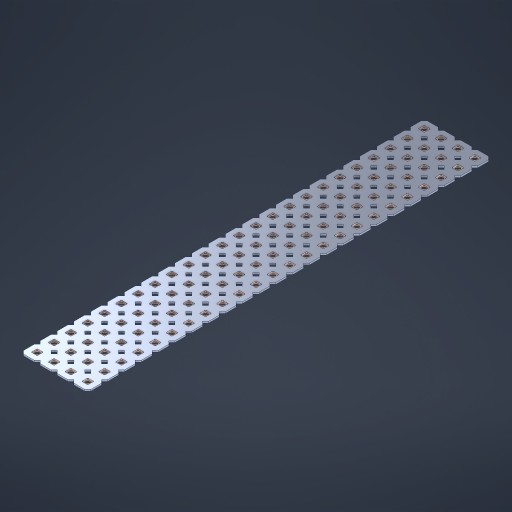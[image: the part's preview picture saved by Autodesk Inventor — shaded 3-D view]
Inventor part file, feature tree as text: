
AUTODESK INVENTOR PART (.ipt)
format: ipt  version: 2023 (Build 270158000, 158)  size: 1,368,064 bytes
history: native  units: in
note: dims shown in document units (in); Inventor stores cm internally (conversion verified against a paired STEP export)
features: other x97, extrude x95, sketch x2, pattern_linear x1
ambient origin geometry x8: Origin, YZ Plane, XZ Plane, XY Plane, X Axis, Y Axis, Z Axis, Center Point
bodies: Solid1 (feature_tree), Body (feature_tree)
feature tree (195):
  pattern_linear  "Rectangular Pattern1"  Spacing1=0.09in  [1 undecoded]
  sketch  "Sketch1"  dims[d1=0.5in]
  sketch  "Sketch2"  dims[d2=0.182in d3=0.09in d4=0.09in d5=0.09in d6=0.09in d7=0.09in d8=0.09in d9=0.09in d10=0.09in d11=0.02in d13=0.0in d14=0.172in d15=0.0625in d16=0.0in d19=0.5in d22=0.5in]
  other  "Srf1"
  other  "Srf126"
  other  "Srf127"
  other  "Srf128"
  other  "Srf129"
  other  "Srf130"
  other  "Srf131"
  other  "Srf250"
  other  "Srf251"
  other  "Srf252"
  other  "Srf253"
  other  "Srf254"
  other  "Srf255"
  other  "Srf256"
  other  "Srf257"
  other  "Srf258"
  other  "Srf259"
  other  "Srf260"
  other  "Srf261"
  other  "Srf262"
  other  "Srf263"
  other  "Srf264"
  other  "Srf265"
  other  "Srf266"
  other  "Srf268"
  other  "Srf269"
  other  "Srf270"
  other  "Srf271"
  other  "Srf272"
  other  "Srf273"
  other  "Srf274"
  other  "Srf275"
  other  "Srf276"
  other  "Srf277"
  other  "Srf278"
  other  "Srf279"
  other  "Srf280"
  other  "Srf281"
  other  "Srf282"
  other  "Srf283"
  other  "Srf284"
  other  "Srf285"
  other  "Srf286"
  other  "Srf287"
  other  "Srf288"
  other  "Srf289"
  other  "Srf290"
  other  "Srf291"
  other  "Srf293"
  other  "Srf294"
  other  "Srf295"
  other  "Srf296"
  other  "Srf297"
  other  "Srf298"
  other  "Srf299"
  other  "Srf300"
  other  "Srf301"
  other  "Srf302"
  other  "Srf303"
  other  "Srf304"
  other  "Srf305"
  other  "Srf306"
  other  "Srf307"
  other  "Srf308"
  other  "Srf309"
  other  "Srf310"
  other  "Srf311"
  other  "Srf312"
  other  "Srf313"
  other  "Srf314"
  other  "Srf315"
  other  "Srf316"
  other  "Srf318"
  other  "Srf319"
  other  "Srf320"
  other  "Srf321"
  other  "Srf322"
  other  "Srf323"
  other  "Srf324"
  other  "Srf325"
  other  "Srf326"
  other  "Srf327"
  other  "Srf328"
  other  "Srf329"
  other  "Srf330"
  other  "Srf331"
  other  "Srf332"
  other  "Srf333"
  other  "Srf334"
  other  "Srf335"
  other  "Srf336"
  other  "Srf337"
  other  "Srf338"
  other  "Srf339"
  other  "Srf340"
  other  "Srf341"
  other  "Circle"
  extrude  "ExtrusionSrf126"  Depth=0.09in
  extrude  "ExtrusionSrf127"  Depth=0.09in
  extrude  "ExtrusionSrf128"  Depth=0.09in
  extrude  "ExtrusionSrf129"  Depth=0.09in
  extrude  "ExtrusionSrf130"  Depth=0.09in
  extrude  "ExtrusionSrf131"  Depth=0.09in
  extrude  "ExtrusionSrf250"  Depth=0.09in
  extrude  "ExtrusionSrf251"  Depth=0.02in
  extrude  "ExtrusionSrf252"  TaperAngle=0.0deg  [1 undecoded]
  extrude  "ExtrusionSrf253"  Depth=0.5in
  extrude  "ExtrusionSrf254"  Depth=0.5in TaperAngle=0.0deg
  extrude  "ExtrusionSrf255"  Depth=0.5in
  extrude  "ExtrusionSrf256"  Depth=0.5in
  extrude  "ExtrusionSrf257"  [1 undecoded]
  extrude  "ExtrusionSrf258"  [1 undecoded]
  extrude  "ExtrusionSrf259"  [1 undecoded]
  extrude  "ExtrusionSrf260"  [1 undecoded]
  extrude  "ExtrusionSrf261"  [1 undecoded]
  extrude  "ExtrusionSrf262"  [1 undecoded]
  extrude  "ExtrusionSrf263"  [1 undecoded]
  extrude  "ExtrusionSrf264"  [1 undecoded]
  extrude  "ExtrusionSrf265"  [1 undecoded]
  extrude  "ExtrusionSrf266"  [1 undecoded]
  extrude  "ExtrusionSrf268"  [1 undecoded]
  extrude  "ExtrusionSrf269"  [1 undecoded]
  extrude  "ExtrusionSrf270"  [1 undecoded]
  extrude  "ExtrusionSrf271"  [1 undecoded]
  extrude  "ExtrusionSrf272"  [1 undecoded]
  extrude  "ExtrusionSrf273"  [1 undecoded]
  extrude  "ExtrusionSrf274"  [1 undecoded]
  extrude  "ExtrusionSrf275"  [1 undecoded]
  extrude  "ExtrusionSrf276"  [1 undecoded]
  extrude  "ExtrusionSrf277"  [1 undecoded]
  extrude  "ExtrusionSrf278"  [1 undecoded]
  extrude  "ExtrusionSrf279"  [1 undecoded]
  extrude  "ExtrusionSrf280"  [1 undecoded]
  extrude  "ExtrusionSrf281"  [1 undecoded]
  extrude  "ExtrusionSrf282"  [1 undecoded]
  extrude  "ExtrusionSrf283"  [1 undecoded]
  extrude  "ExtrusionSrf284"  [1 undecoded]
  extrude  "ExtrusionSrf285"  [1 undecoded]
  extrude  "ExtrusionSrf286"  [1 undecoded]
  extrude  "ExtrusionSrf287"  [1 undecoded]
  extrude  "ExtrusionSrf288"  [1 undecoded]
  extrude  "ExtrusionSrf289"  [1 undecoded]
  extrude  "ExtrusionSrf290"  [1 undecoded]
  extrude  "ExtrusionSrf291"  [1 undecoded]
  extrude  "ExtrusionSrf293"  [1 undecoded]
  extrude  "ExtrusionSrf294"  [1 undecoded]
  extrude  "ExtrusionSrf295"  [1 undecoded]
  extrude  "ExtrusionSrf296"  [1 undecoded]
  extrude  "ExtrusionSrf297"  [1 undecoded]
  extrude  "ExtrusionSrf298"  [1 undecoded]
  extrude  "ExtrusionSrf299"  [1 undecoded]
  extrude  "ExtrusionSrf300"  [1 undecoded]
  extrude  "ExtrusionSrf301"  [1 undecoded]
  extrude  "ExtrusionSrf302"  [1 undecoded]
  extrude  "ExtrusionSrf303"  [1 undecoded]
  extrude  "ExtrusionSrf304"  [1 undecoded]
  extrude  "ExtrusionSrf305"  [1 undecoded]
  extrude  "ExtrusionSrf306"  [1 undecoded]
  extrude  "ExtrusionSrf307"  [1 undecoded]
  extrude  "ExtrusionSrf308"  [1 undecoded]
  extrude  "ExtrusionSrf309"  [1 undecoded]
  extrude  "ExtrusionSrf310"  [1 undecoded]
  extrude  "ExtrusionSrf311"  [1 undecoded]
  extrude  "ExtrusionSrf312"  [1 undecoded]
  extrude  "ExtrusionSrf313"  [1 undecoded]
  extrude  "ExtrusionSrf314"  [1 undecoded]
  extrude  "ExtrusionSrf315"  [1 undecoded]
  extrude  "ExtrusionSrf316"  [1 undecoded]
  extrude  "ExtrusionSrf318"  [1 undecoded]
  extrude  "ExtrusionSrf319"  [1 undecoded]
  extrude  "ExtrusionSrf320"  [1 undecoded]
  extrude  "ExtrusionSrf321"  [1 undecoded]
  extrude  "ExtrusionSrf322"  [1 undecoded]
  extrude  "ExtrusionSrf323"  [1 undecoded]
  extrude  "ExtrusionSrf324"  [1 undecoded]
  extrude  "ExtrusionSrf325"  [1 undecoded]
  extrude  "ExtrusionSrf326"  [1 undecoded]
  extrude  "ExtrusionSrf327"  [1 undecoded]
  extrude  "ExtrusionSrf328"  [1 undecoded]
  extrude  "ExtrusionSrf329"  [1 undecoded]
  extrude  "ExtrusionSrf330"  [1 undecoded]
  extrude  "ExtrusionSrf331"  [1 undecoded]
  extrude  "ExtrusionSrf332"  [1 undecoded]
  extrude  "ExtrusionSrf333"  [1 undecoded]
  extrude  "ExtrusionSrf334"  [1 undecoded]
  extrude  "ExtrusionSrf335"  [1 undecoded]
  extrude  "ExtrusionSrf336"  [1 undecoded]
  extrude  "ExtrusionSrf337"  [1 undecoded]
  extrude  "ExtrusionSrf338"  [1 undecoded]
  extrude  "ExtrusionSrf339"  [1 undecoded]
  extrude  "ExtrusionSrf340"  [1 undecoded]
  extrude  "ExtrusionSrf341"  [1 undecoded]
note: 84 required parameter values undecoded (feature->parameter linkage not recoverable at this tier; creation-order binding heuristic only, values carry confidence <= 0.55)
